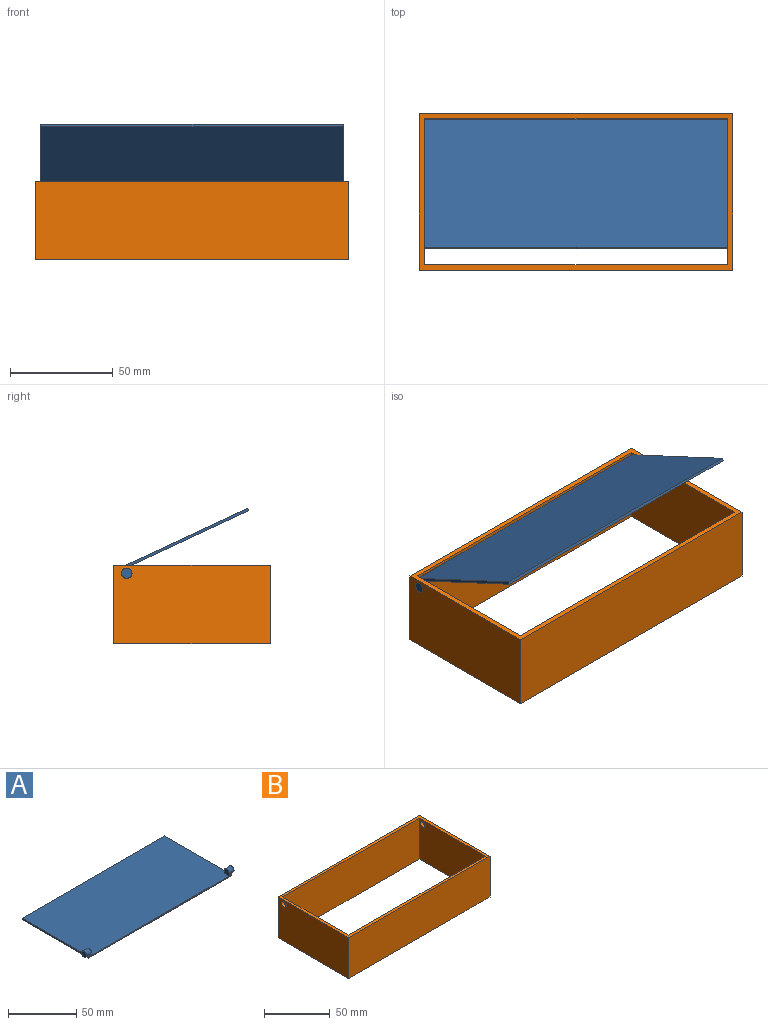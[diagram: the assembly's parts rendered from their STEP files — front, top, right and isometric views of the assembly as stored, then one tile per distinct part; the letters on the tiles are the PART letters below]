
ASSEMBLY  parts=2 mates=1
PART A: 15 faces, bbox 152.4x69.2x6.4 mm
  f0: plane 147.32x69.22mm, normal (0,0,1), area 10170.9mm2, adj f1,f2,f3,f4,f6,f7,f8,f9
  f1: plane 69.22x3.81mm, normal (-1,0,0), area 90.6mm2, adj f0,f2,f4,f5,f8,f12,f14
  f2: plane 147.32x3.18mm, normal (0,-1,0), area 106.5mm2, adj f0,f1,f3,f7,f9,f10,f12,f14
  f3: plane 69.22x3.81mm, normal (1,0,0), area 90.6mm2, adj f0,f2,f4,f5,f6,f10,f14
  f4: plane 147.32x1.27mm, normal (0,1,0), area 187.1mm2, adj f0,f1,f3,f5
  f5: plane 147.32x68.58mm, normal (0,0,-1), area 10103.2mm2, adj f1,f3,f4,f14
  f6: plane 2.54x2.54mm, normal (0,1,0), area 6.5mm2, adj f0,f3,f7,f10
  f7: plane 5.08x5.08mm, normal (-1,0,0), area 23mm2, adj f0,f2,f6,f10
  f8: plane 2.54x2.54mm, normal (0,1,0), area 6.5mm2, adj f0,f1,f9,f12
  f9: plane 5.08x5.08mm, normal (1,0,0), area 23mm2, adj f0,f2,f8,f12
  f10: cylinder r=2.54mm len=5.08mm, axis (-1,0,0), area 60.8mm2, adj f2,f3,f6,f7,f11
  f11: plane 5.08x5.08mm, normal (1,0,0), area 20.3mm2, adj f10
  f12: cylinder r=2.54mm len=5.08mm, axis (1,0,0), area 60.8mm2, adj f1,f2,f8,f9,f13
  f13: plane 5.08x5.08mm, normal (-1,0,0), area 20.3mm2, adj f12
  f14: cylinder r=0.64mm len=147.32mm, axis (1,0,0), area 146.9mm2, adj f1,f2,f3,f5
PART B: 12 faces, bbox 152.4x76.2x38.1 mm
  f0: plane 152.4x76.2mm, normal (0,0,1), area 1135.5mm2, adj f2,f3,f4,f5,f6,f7,f8,f9
  f1: plane 152.4x76.2mm, normal (0,0,-1), area 1135.5mm2, adj f2,f3,f4,f5,f6,f7,f8,f9
  f2: plane 76.2x38.1mm, normal (-1,0,0), area 2883mm2, adj f0,f1,f3,f5,f10
  f3: plane 152.4x38.1mm, normal (0,-1,0), area 5806.4mm2, adj f0,f1,f2,f4
  f4: plane 76.2x38.1mm, normal (1,0,0), area 2883mm2, adj f0,f1,f3,f5,f11
  f5: plane 152.4x38.1mm, normal (0,1,0), area 5806.4mm2, adj f0,f1,f2,f4
  f6: plane 147.32x38.1mm, normal (0,-1,0), area 5612.9mm2, adj f0,f1,f7,f9
  f7: plane 71.12x38.1mm, normal (1,0,0), area 2689.4mm2, adj f0,f1,f6,f8,f10
  f8: plane 147.32x38.1mm, normal (0,1,0), area 5612.9mm2, adj f0,f1,f7,f9
  f9: plane 71.12x38.1mm, normal (-1,0,0), area 2689.4mm2, adj f0,f1,f6,f8,f11
  f10: cylinder r=2.54mm len=5.08mm, axis (1,0,0), area 40.5mm2, adj f2,f7
  f11: cylinder r=2.54mm len=5.08mm, axis (-1,0,0), area 40.5mm2, adj f4,f9
PLACE A rot(axis=(1,0,0),155deg) t=(-43.9,33.93,27.84)mm
PLACE B t=(-46.44,-39.84,-8.83)mm
MATE revolute A.f10 <-> B.f10  axis (1,0,0) through (105.96,30.01,25.46)mm
